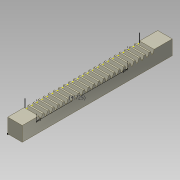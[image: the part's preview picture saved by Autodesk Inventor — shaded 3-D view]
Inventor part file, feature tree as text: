
AUTODESK INVENTOR PART (.ipt)
format: ipt  version: 2012 SP2 (Build 160219200, 219)  size: 312,832 bytes
history: native  units: mm (DEFAULTED — no unit token found)
features: sketch x8, plane x6, extrude x3, projected_geometry x3
ambient origin geometry x8: Origin, YZ Plane, XZ Plane, XY Plane, X Axis, Y Axis, Z Axis, Center Point
bodies: Solid1 (feature_tree)
feature tree (20):
  extrude  "Extrusion1"  Depth=19.05mm
  extrude  "Extrusion2"  Depth=2.11582mm
  extrude  "Extrusion3"  Depth=3.490659mm
  plane  "Work Plane1"
  plane  "Work Plane2"
  sketch  "Sketch6"  dims[d11=6.64972mm]
  plane  "Work Plane3"
  sketch  "Sketch7"  dims[d12=3.32486mm]
  plane  "Work Plane4"
  plane  "Work Plane5"
  sketch  "Sketch8"  dims[d13=3.32486mm]
  sketch  "Sketch9"  dims[d14=3.32486mm]
  sketch  "Sketch10"  dims[d15=23.7998mm d16=2.44856mm d17=210.0mm d19=6.6548mm d20=10.0mm d22=25.4mm d24=25.4mm d25=0.0mm d26=1.5494mm d27=1.905mm d28=25.4mm d29=0.0mm d30=149.847577mm d32=120.023623mm d33=120.023623mm]
  plane  "Work Plane7"
  sketch  "Sketch1"  dims[d0=19.05mm d1=19.05mm]
  sketch  "Sketch2"  dims[d2=196.85mm d3=0.0mm d5=2.11582mm]
  projected_geometry  "Projected Loop1"
  sketch  "Sketch5"  dims[d6=3.490659mm d7=3.490659mm]
  projected_geometry  "Projected Loop4"
  projected_geometry  "Projected Loop6"
